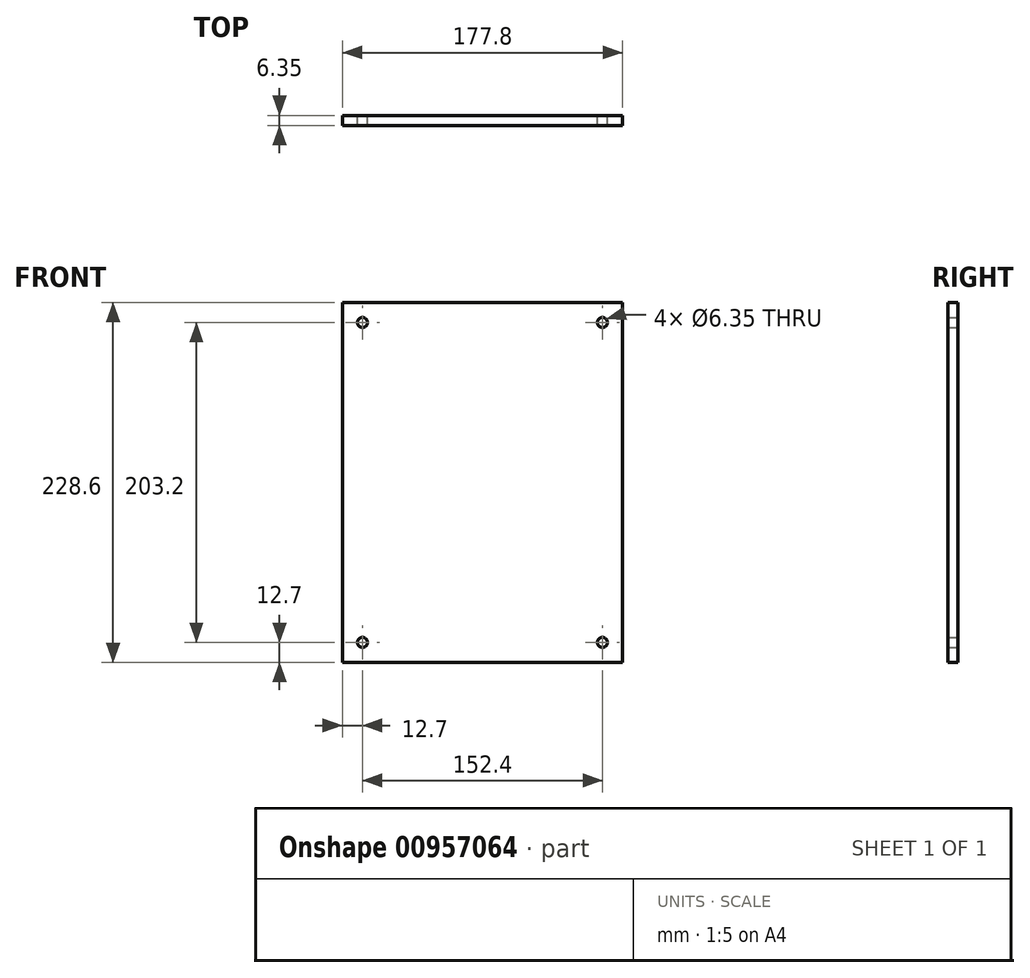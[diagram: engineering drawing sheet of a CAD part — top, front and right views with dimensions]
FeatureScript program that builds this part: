
annotation { "Feature Type Name" : "Feature", "Feature Type Description" : "" }
export const myFeature = defineFeature(function(context is Context, id is Id, definition is map)
    precondition{}
    {
        {
            var Q0;
            Q0=qCreatedBy(makeId("Front.planeOp"),FACE);
            var sketch = newSketch(context, id + "F0", { "sketchPlane" : qUnion([Q0])});
            skLineSegment(sketch, "E0.bottom", {"start": v(88.9, 114.3) * mm, "end": v(-88.9, 114.3) * mm});
            skLineSegment(sketch, "E0.top", {"start": v(88.9, -114.3) * mm, "end": v(-88.9, -114.3) * mm});
            skLineSegment(sketch, "E0.left", {"start": v(88.9, 114.3) * mm, "end": v(88.9, -114.3) * mm});
            skLineSegment(sketch, "E0.right", {"start": v(-88.9, 114.3) * mm, "end": v(-88.9, -114.3) * mm});
            skPoint(sketch, "E0.middle", {"position": v(0, 0) * mm});
            skCircle(sketch, "E1", {"center": v(-76.2, 101.6) * mm, "radius": 3.18 * mm});
            skCircle(sketch, "E2", {"center": v(76.2, 101.6) * mm, "radius": 3.18 * mm});
            skCircle(sketch, "E3", {"center": v(76.2, -101.6) * mm, "radius": 3.18 * mm});
            skCircle(sketch, "E4", {"center": v(-76.2, -101.6) * mm, "radius": 3.18 * mm});
            skSolve(sketch);
        }
        {
            var Q0;
            Q0 = qSketchRegion(id + "F0", true);
            extrude(context, id + "F1", {"entities" : qUnion([Q0]), "depth" : 6.35 * mm, "offsetDistance" : 25.4 * mm});
        }
    });
